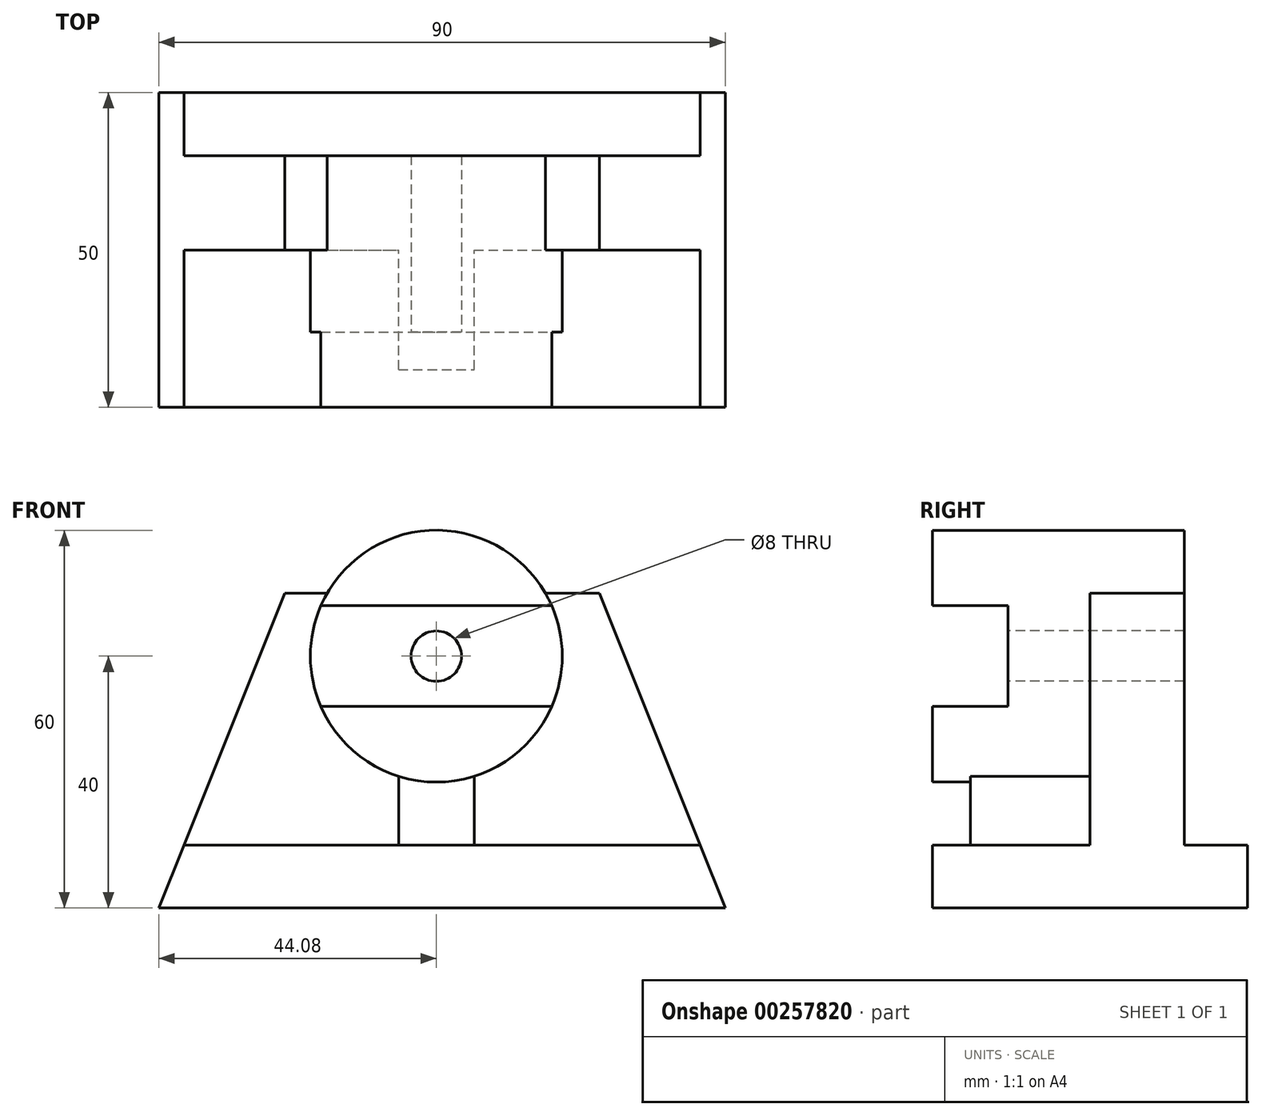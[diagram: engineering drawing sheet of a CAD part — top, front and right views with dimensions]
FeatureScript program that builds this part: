
annotation { "Feature Type Name" : "Feature", "Feature Type Description" : "" }
export const myFeature = defineFeature(function(context is Context, id is Id, definition is map)
    precondition{}
    {
        {
            var Q0;
            Q0=qCreatedBy(makeId("Top.planeOp"),FACE);
            var sketch = newSketch(context, id + "F0", { "sketchPlane" : qUnion([Q0])});
            skLineSegment(sketch, "E0.bottom", {"start": v(-44.08, 35.87) * mm, "end": v(45.92, 35.87) * mm});
            skLineSegment(sketch, "E0.top", {"start": v(-44.08, -14.13) * mm, "end": v(45.92, -14.13) * mm});
            skLineSegment(sketch, "E0.left", {"start": v(-44.08, 35.87) * mm, "end": v(-44.08, -14.13) * mm});
            skLineSegment(sketch, "E0.right", {"start": v(45.92, 35.87) * mm, "end": v(45.92, -14.13) * mm});
            skSolve(sketch);
        }
        {
            var Q0;
            Q0=makeQuery(id+"F0.imprint","IMPRINT",FACE,{"disambiguationData":[TD([[makeQuery(id+"F0.imprint","IMPRINT",EDGE,{"derivedFrom":sQuery(id+"F0.wireOp",EDGE,"E0.bottom")}),-1.0]])]});
            extrude(context, id + "F1", {"entities" : qUnion([Q0]), "depth" : 10 * mm});
        }
        {
            var Q0;
            Q0=makeQuery(id+"F1.opExtrude","CAP_FACE",FACE,{"disambiguationData":[OSD([sQuery(id+"F0.wireOp",EDGE,"E0.bottom"),sQuery(id+"F0.wireOp",EDGE,"E0.top"),sQuery(id+"F0.wireOp",EDGE,"E0.left"),sQuery(id+"F0.wireOp",EDGE,"E0.right")])],"isStart":false});
            var sketch = newSketch(context, id + "F2", { "sketchPlane" : qUnion([Q0])});
            skLineSegment(sketch, "E1", {"start": v(-44.08, 25.87) * mm, "end": v(45.92, 25.87) * mm});
            skLineSegment(sketch, "E2", {"start": v(-44.08, 10.87) * mm, "end": v(45.92, 10.87) * mm});
            skSolve(sketch);
        }
        {
            var Q0;
            {var subQ0=sQuery(id+"F2.wireOp",EDGE,"E1");Q0=makeQuery(id+"F2.imprint","IMPRINT",FACE,{"disambiguationData":[TD([[makeQuery(id+"F2.imprint","IMPRINT",EDGE,{"derivedFrom":subQ0}),-1.0]])]});}
            extrude(context, id + "F3", {"entities" : qUnion([Q0]), "operationType" : NewBodyOperationType.ADD, "depth" : 40 * mm});
        }
        {
            var Q0;
            Q0=makeQuery(id+"F3.opExtrude","CAP_EDGE",EDGE,{"disambiguationData":[OSD([sQuery(id+"F0.wireOp",EDGE,"E0.left")])],"isStart":false});
            chamfer(context, id + "F4", {"entities" : qUnion([Q0]), "chamferType" : ChamferType.TWO_OFFSETS, "width1" : 20 * mm, "oppositeDirection" : false, "width2" : 50 * mm, "tangentPropagation" : true});
        }
        {
            var Q0;
            Q0=makeQuery(id+"F3.opExtrude","CAP_EDGE",EDGE,{"disambiguationData":[OSD([sQuery(id+"F0.wireOp",EDGE,"E0.right")])],"isStart":false});
            chamfer(context, id + "F5", {"entities" : qUnion([Q0]), "chamferType" : ChamferType.TWO_OFFSETS, "width1" : 50 * mm, "oppositeDirection" : false, "width2" : 20 * mm, "tangentPropagation" : true});
        }
        {
            var Q0;
            Q0=makeQuery(id+"F3.opExtrude","SWEPT_FACE",FACE,{"disambiguationData":[OSD([sQuery(id+"F2.wireOp",EDGE,"E2")])]});
            var sketch = newSketch(context, id + "F6", { "sketchPlane" : qUnion([Q0])});
            skCircle(sketch, "E3", {"center": v(0, 40) * mm, "radius": 20 * mm});
            skLineSegment(sketch, "E4", {"start": v(-18.33, 32) * mm, "end": v(18.33, 32) * mm});
            skLineSegment(sketch, "E5", {"start": v(-18.33, 48) * mm, "end": v(18.33, 48) * mm});
            skLineSegment(sketch, "E6", {"start": v(-6, 20.92) * mm, "end": v(-6, 10) * mm});
            skLineSegment(sketch, "E7", {"start": v(6, 20.92) * mm, "end": v(6, 10) * mm});
            skSolve(sketch);
        }
        {
            var Q0;
            {var subQ0=sQuery(id+"F6.wireOp",EDGE,"E3");var subQ1=makeQuery(id+"F3.opExtrude","CAP_EDGE",EDGE,{"disambiguationData":[OSD([sQuery(id+"F2.wireOp",EDGE,"E2")])],"isStart":false});var subQ2=makeQuery(id+"F6.imprint","INTERSECT",VERTEX,{"disambiguationData":[OD(0.0)],"derivedFrom":[subQ1,subQ0]});Q0=makeQuery(id+"F6.imprint","IMPRINT",FACE,{"disambiguationData":[TD([[makeQuery(id+"F6.imprint","IMPRINT",EDGE,{"disambiguationData":[TD([[subQ2,-1.0]])],"derivedFrom":subQ0}),1.0]])]});}
            var Q1;
            {var subQ0=sQuery(id+"F6.wireOp",EDGE,"E5");Q1=makeQuery(id+"F6.imprint","IMPRINT",FACE,{"disambiguationData":[TD([[makeQuery(id+"F6.imprint","IMPRINT",EDGE,{"derivedFrom":subQ0}),1.0]])]});}
            var Q2;
            {var subQ0=sQuery(id+"F6.wireOp",EDGE,"E4");Q2=makeQuery(id+"F6.imprint","IMPRINT",FACE,{"disambiguationData":[TD([[makeQuery(id+"F6.imprint","IMPRINT",EDGE,{"derivedFrom":subQ0}),-1.0]])]});}
            extrude(context, id + "F7", {"entities" : qUnion([Q0, Q1, Q2]), "operationType" : NewBodyOperationType.ADD, "depth" : 25 * mm});
        }
        {
            var Q0;
            Q0=makeQuery(id+"F7.opExtrude","CAP_FACE",FACE,{"disambiguationData":[OSD([sQuery(id+"F6.wireOp",EDGE,"E3"),sQuery(id+"F6.wireOp",EDGE,"E5")])],"isStart":true});
            extrude(context, id + "F8", {"entities" : qUnion([Q0]), "operationType" : NewBodyOperationType.ADD, "depth" : 15 * mm});
        }
        {
            var Q0;
            {var subQ0=sQuery(id+"F6.wireOp",EDGE,"E4");Q0=makeQuery(id+"F6.imprint","IMPRINT",FACE,{"disambiguationData":[TD([[makeQuery(id+"F6.imprint","IMPRINT",EDGE,{"derivedFrom":subQ0}),1.0]])]});}
            extrude(context, id + "F9", {"entities" : qUnion([Q0]), "operationType" : NewBodyOperationType.ADD, "depth" : 13 * mm});
        }
        {
            var Q0;
            {var subQ0=sQuery(id+"F6.wireOp",EDGE,"E6");Q0=makeQuery(id+"F6.imprint","IMPRINT",FACE,{"disambiguationData":[TD([[makeQuery(id+"F6.imprint","IMPRINT",EDGE,{"derivedFrom":subQ0}),1.0]])]});}
            extrude(context, id + "F10", {"entities" : qUnion([Q0]), "operationType" : NewBodyOperationType.ADD, "depth" : 19 * mm});
        }
        {
            var Q0;
            Q0=makeQuery(id+"F9.opExtrude","CAP_FACE",FACE,{"disambiguationData":[OSD([sQuery(id+"F6.wireOp",EDGE,"E3"),sQuery(id+"F6.wireOp",EDGE,"E4"),sQuery(id+"F6.wireOp",EDGE,"E5")])],"isStart":false});
            var sketch = newSketch(context, id + "F11", { "sketchPlane" : qUnion([Q0])});
            skCircle(sketch, "E8", {"center": v(0, 40) * mm, "radius": 4 * mm});
            skSolve(sketch);
        }
        {
            var Q0;
            Q0=makeQuery(id+"F11.imprint","IMPRINT",FACE,{"disambiguationData":[TD([[makeQuery(id+"F11.imprint","IMPRINT",EDGE,{"derivedFrom":sQuery(id+"F11.wireOp",EDGE,"E8")}),1.0]])]});
            extrude(context, id + "F12", {"entities" : qUnion([Q0]), "operationType" : NewBodyOperationType.REMOVE, "oppositeDirection" : true, "depth" : 40 * mm});
        }
    });
